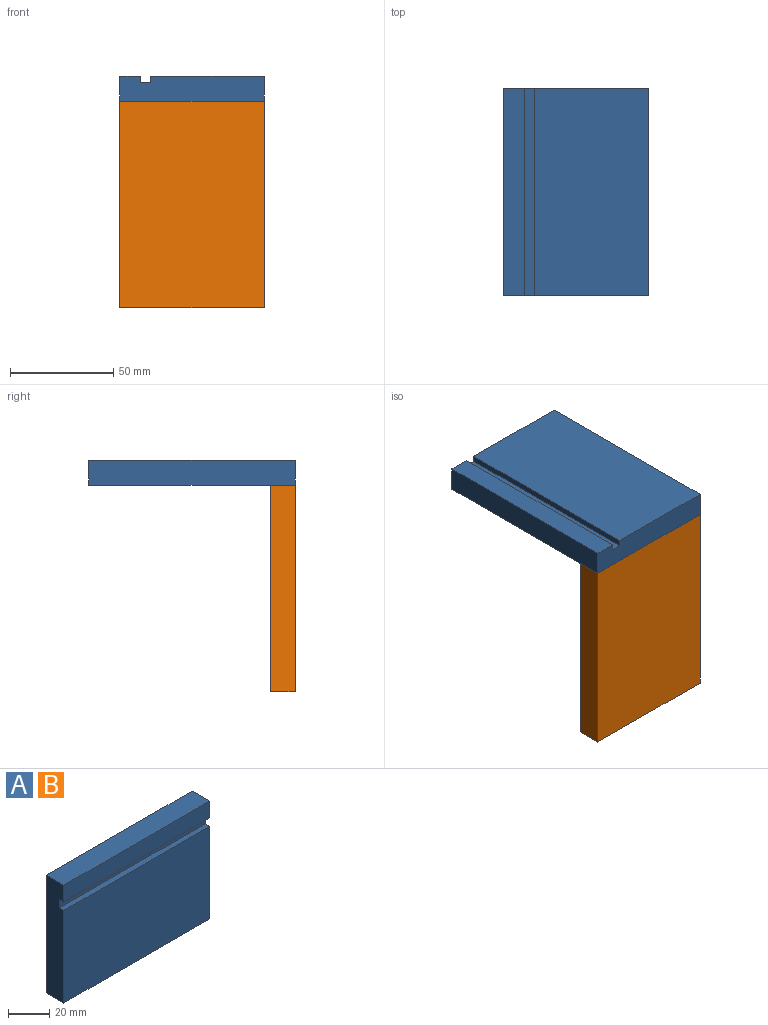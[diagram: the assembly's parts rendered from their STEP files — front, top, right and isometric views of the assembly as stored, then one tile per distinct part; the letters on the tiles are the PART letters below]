
ASSEMBLY  parts=2 mates=1
PART A: 10 faces, bbox 100x12x70 mm
  f0: plane 100x70mm, normal (0,1,0), area 7000mm2, adj f1,f6,f8,f9
  f1: plane 100x12mm, normal (0,0,1), area 1200mm2, adj f0,f7,f8,f9
  f2: plane 100x3mm, normal (0,0,-1), area 300mm2, adj f3,f7,f8,f9
  f3: plane 100x5mm, normal (0,-1,0), area 500mm2, adj f2,f4,f8,f9
  f4: plane 100x3mm, normal (0,0,1), area 300mm2, adj f3,f5,f8,f9
  f5: plane 100x55mm, normal (0,-1,0), area 5500mm2, adj f4,f6,f8,f9
  f6: plane 100x12mm, normal (0,0,-1), area 1200mm2, adj f0,f5,f8,f9
  f7: plane 100x10mm, normal (0,-1,0), area 1000mm2, adj f1,f2,f8,f9
  f8: plane 70x12mm, normal (-1,0,0), area 825mm2, adj f0,f1,f2,f3,f4,f5,f6,f7
  f9: plane 70x12mm, normal (1,0,0), area 825mm2, adj f0,f1,f2,f3,f4,f5,f6,f7
PART B: same geometry as A
PLACE A rot(axis=(-0.58,-0.58,0.58),120deg) t=(-45.46,-61.49,13.2)mm
PLACE B rot(axis=(0.71,0,-0.71),180deg) t=(-45.46,-61.49,13.2)mm
MATE revolute A.f1 <-> B.f1  axis (-1,0,0) through (-115.46,-61.49,13.2)mm
